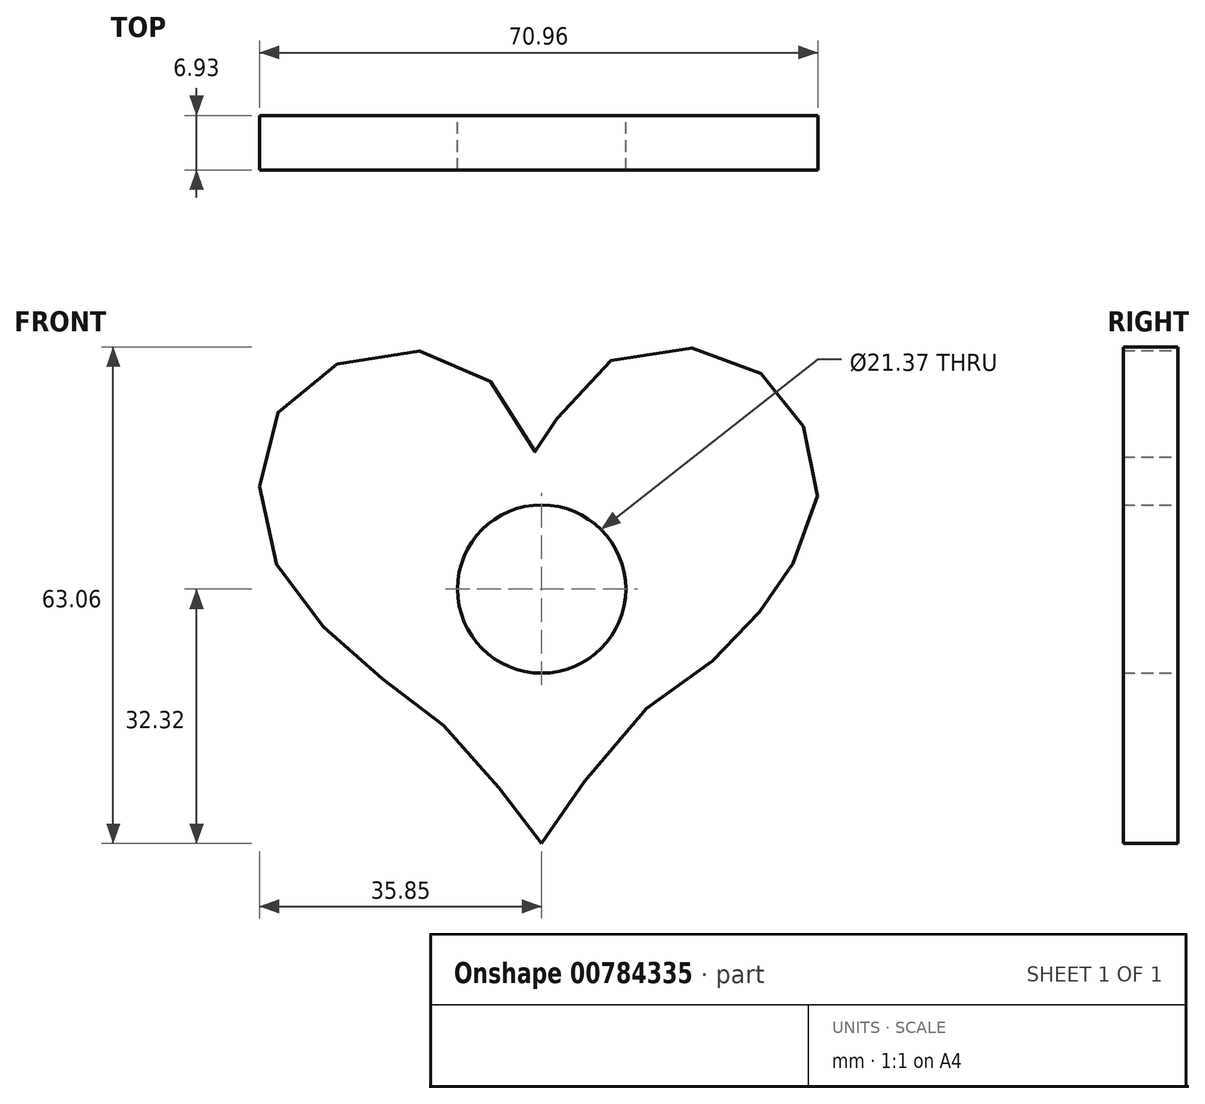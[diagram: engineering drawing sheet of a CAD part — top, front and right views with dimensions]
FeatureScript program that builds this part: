
annotation { "Feature Type Name" : "Feature", "Feature Type Description" : "" }
export const myFeature = defineFeature(function(context is Context, id is Id, definition is map)
    precondition{}
    {
        {
            var Q0;
            Q0=qCreatedBy(makeId("Front.planeOp"),FACE);
            var sketch = newSketch(context, id + "F0", { "sketchPlane" : qUnion([Q0])});
            skCircle(sketch, "E0", {"center": v(0, 0) * mm, "radius": 10.69 * mm});
            skFitSpline(sketch, "E1", {"points": [v(0, -32.32) * mm, v(7.8, -20.6) * mm, v(19.77, -10.68) * mm, v(27.15, -3.56) * mm, v(31.22, 2.04) * mm, v(35.04, 11.71) * mm, v(32.75, 21.64) * mm, v(26.13, 28.51) * mm, v(14.17, 30.55) * mm, v(2.97, 23.93) * mm, v(0, 16.8) * mm, v(-5.94, 25.71) * mm, v(-17.38, 30.29) * mm, v(-30.4, 26.03) * mm, v(-35.65, 16.02) * mm, v(-33.7, 3.24) * mm, v(-25.84, -6.6) * mm, v(-16.24, -14.48) * mm, v(-6.64, -23.34) * mm, v(0, -32.32) * mm]});
            skSolve(sketch);
        }
        {
            var Q0;
            Q0=makeQuery(id+"F0.imprint","IMPRINT",FACE,{"disambiguationData":[TD([[makeQuery(id+"F0.imprint","IMPRINT",EDGE,{"derivedFrom":sQuery(id+"F0.wireOp",EDGE,"E0")}),-1.0]])]});
            extrude(context, id + "F1", {"entities" : qUnion([Q0]), "depth" : 6.93 * mm, "offsetDistance" : 25.4 * mm});
        }
    });
